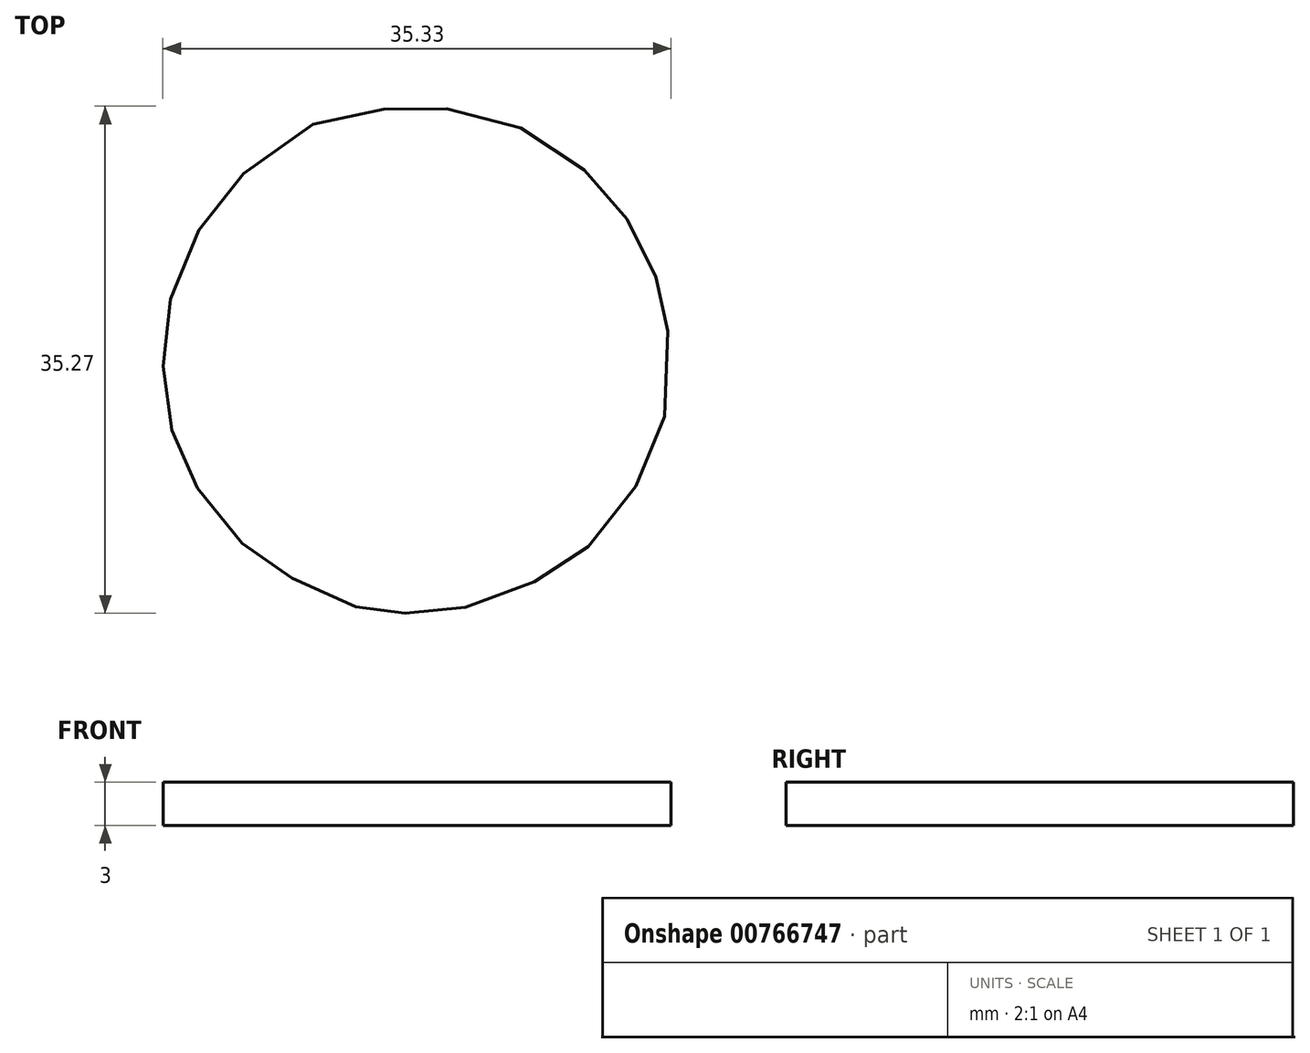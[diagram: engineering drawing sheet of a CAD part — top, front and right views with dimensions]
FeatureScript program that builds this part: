
annotation { "Feature Type Name" : "Feature", "Feature Type Description" : "" }
export const myFeature = defineFeature(function(context is Context, id is Id, definition is map)
    precondition{}
    {
        {
            var Q0;
            Q0=qCreatedBy(makeId("Top.planeOp"),FACE);
            var sketch = newSketch(context, id + "F0", { "sketchPlane" : qUnion([Q0])});
            skFitSpline(sketch, "E0", {"points": [v(-6.53, 19.03) * mm, v(-10.42, 16.47) * mm, v(-13.23, 13.52) * mm, v(-14.82, 11.04) * mm, v(-16.25, 7.48) * mm, v(-16.8, 5.2) * mm, v(-16.95, 1.73) * mm, v(-16.6, -1) * mm, v(-16.06, -3.22) * mm, v(-14.92, -5.64) * mm, v(-13.43, -7.92) * mm, v(-11.06, -10.5) * mm, v(-9.37, -11.73) * mm, v(-6.9, -13.12) * mm, v(-3.97, -14.4) * mm, v(-1.8, -14.9) * mm, v(-0.88, -14.96) * mm, v(1.44, -14.96) * mm, v(3.5, -14.69) * mm, v(6.88, -13.69) * mm, v(9.62, -12.39) * mm, v(11.6, -11.16) * mm, v(14.38, -8.47) * mm, v(16.24, -5.53) * mm, v(17.63, -2.23) * mm, v(18.36, 2.37) * mm, v(17.87, 6.1) * mm, v(17.58, 7.26) * mm, v(16.8, 9.8) * mm, v(15.52, 12.08) * mm, v(14.3, 13.88) * mm, v(11.9, 16.2) * mm, v(8.6, 18.36) * mm, v(6.1, 19.49) * mm, v(1.88, 20.22) * mm, v(0, 20.26) * mm, v(-3.58, 19.8) * mm, v(-6.53, 19.03) * mm]});
            skSolve(sketch);
        }
        {
            var Q0;
            Q0=makeQuery(id+"F0.imprint","IMPRINT",FACE,{"disambiguationData":[TD([[makeQuery(id+"F0.imprint","IMPRINT",EDGE,{"derivedFrom":sQuery(id+"F0.wireOp",EDGE,"E0")}),1.0]])]});
            extrude(context, id + "F1", {"entities" : qUnion([Q0]), "depth" : 3 * mm, "offsetDistance" : 25 * mm});
        }
    });
